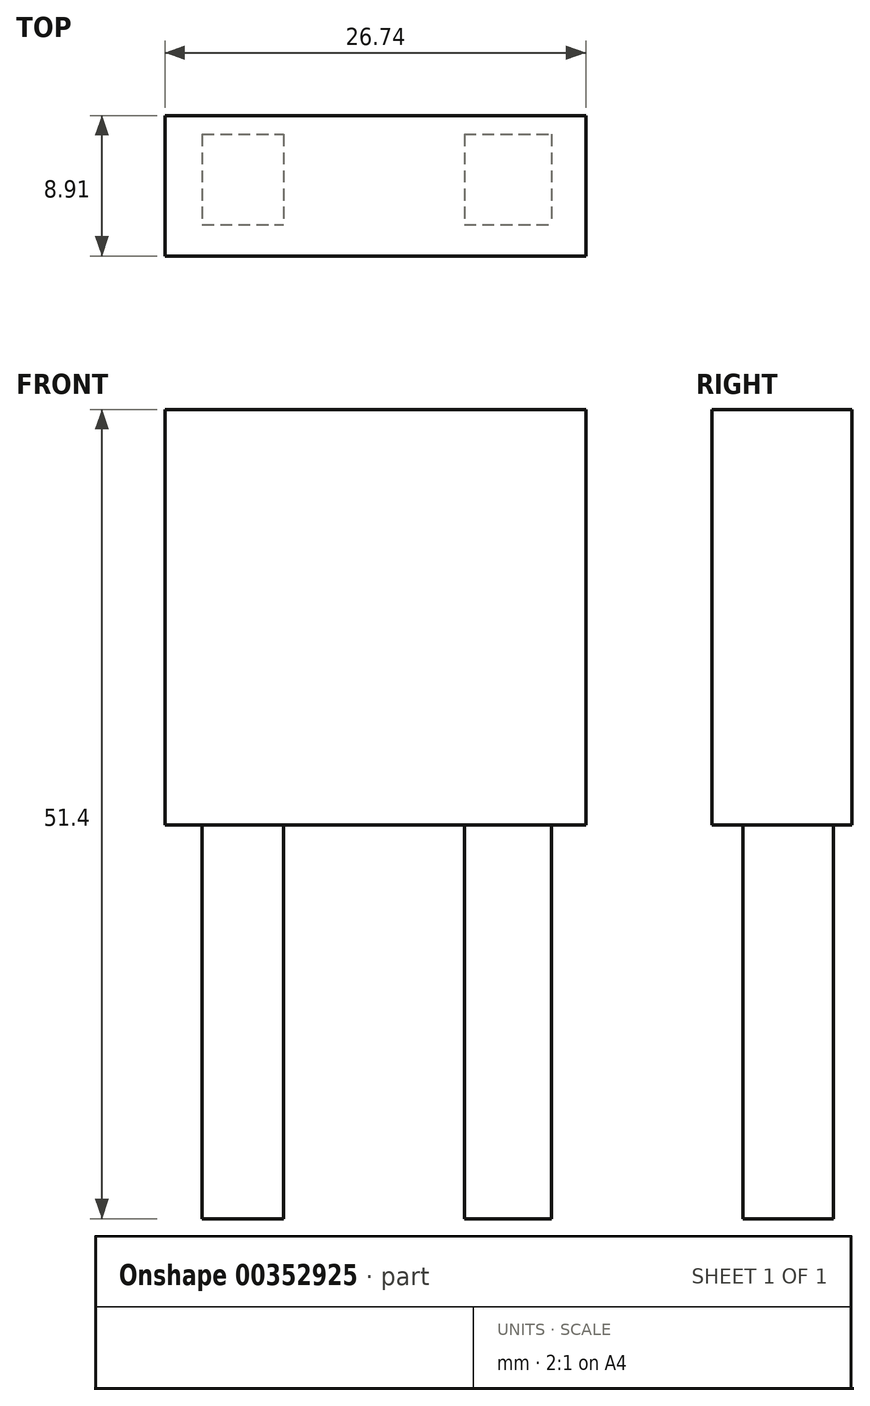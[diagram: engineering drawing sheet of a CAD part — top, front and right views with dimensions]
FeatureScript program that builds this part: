
annotation { "Feature Type Name" : "Feature", "Feature Type Description" : "" }
export const myFeature = defineFeature(function(context is Context, id is Id, definition is map)
    precondition{}
    {
        {
            var Q0;
            Q0=qCreatedBy(makeId("Top.planeOp"),FACE);
            var sketch = newSketch(context, id + "F0", { "sketchPlane" : qUnion([Q0])});
            skLineSegment(sketch, "E0.bottom", {"start": v(-30.9, 14.36) * mm, "end": v(-25.75, 14.36) * mm});
            skLineSegment(sketch, "E0.top", {"start": v(-30.9, 8.62) * mm, "end": v(-25.75, 8.62) * mm});
            skLineSegment(sketch, "E0.left", {"start": v(-30.9, 14.36) * mm, "end": v(-30.9, 8.62) * mm});
            skLineSegment(sketch, "E0.right", {"start": v(-25.75, 14.36) * mm, "end": v(-25.75, 8.62) * mm});
            skLineSegment(sketch, "E1.bottom", {"start": v(-14.26, 14.36) * mm, "end": v(-8.72, 14.36) * mm});
            skLineSegment(sketch, "E1.top", {"start": v(-14.26, 8.62) * mm, "end": v(-8.72, 8.62) * mm});
            skLineSegment(sketch, "E1.left", {"start": v(-14.26, 14.36) * mm, "end": v(-14.26, 8.62) * mm});
            skLineSegment(sketch, "E1.right", {"start": v(-8.72, 14.36) * mm, "end": v(-8.72, 8.62) * mm});
            skSolve(sketch);
        }
        {
            var Q0;
            Q0 = qSketchRegion(id + "F0", true);
            extrude(context, id + "F1", {"entities" : qUnion([Q0]), "depth" : 25 * mm});
        }
        {
            var Q0;
            Q0=makeQuery(id+"F1.opExtrude","CAP_FACE",FACE,{"disambiguationData":[OSD([sQuery(id+"F0.wireOp",EDGE,"E0.bottom"),sQuery(id+"F0.wireOp",EDGE,"E0.top"),sQuery(id+"F0.wireOp",EDGE,"E0.left"),sQuery(id+"F0.wireOp",EDGE,"E0.right")])],"isStart":false});
            var sketch = newSketch(context, id + "F2", { "sketchPlane" : qUnion([Q0])});
            skLineSegment(sketch, "E2.bottom", {"start": v(-33.28, 15.55) * mm, "end": v(-6.54, 15.55) * mm});
            skLineSegment(sketch, "E2.top", {"start": v(-33.28, 6.64) * mm, "end": v(-6.54, 6.64) * mm});
            skLineSegment(sketch, "E2.left", {"start": v(-33.28, 15.55) * mm, "end": v(-33.28, 6.64) * mm});
            skLineSegment(sketch, "E2.right", {"start": v(-6.54, 15.55) * mm, "end": v(-6.54, 6.64) * mm});
            skSolve(sketch);
        }
        {
            var Q0;
            Q0 = qSketchRegion(id + "F2", true);
            extrude(context, id + "F3", {"entities" : qUnion([Q0]), "depth" : 26.4 * mm});
        }
    });
